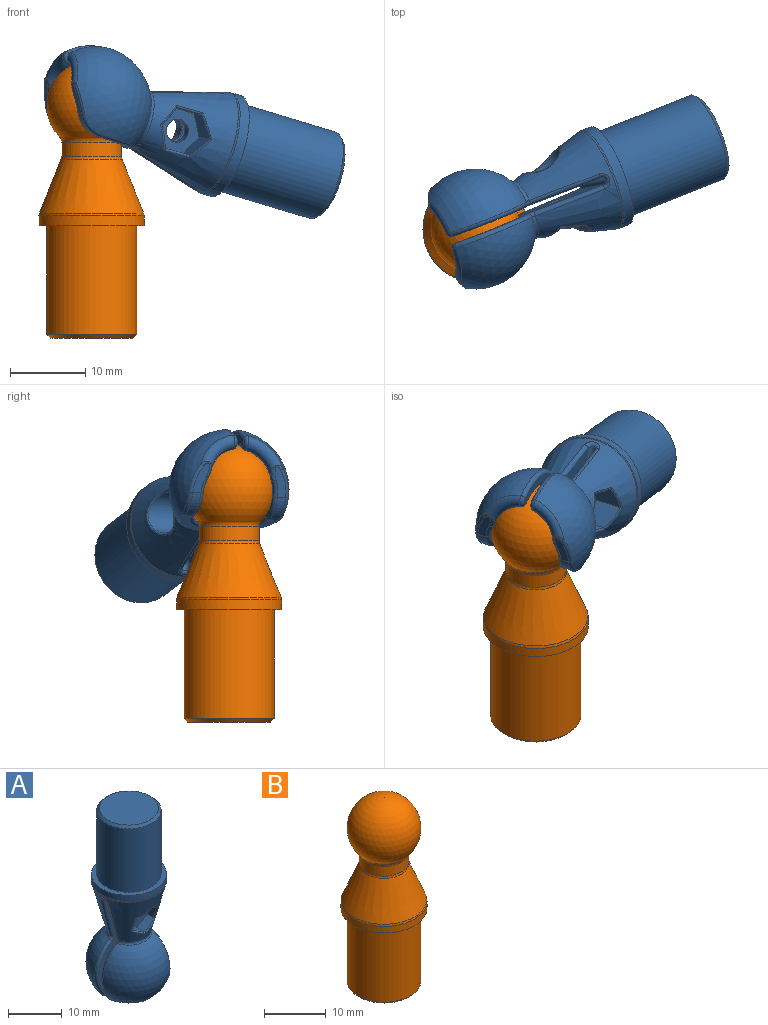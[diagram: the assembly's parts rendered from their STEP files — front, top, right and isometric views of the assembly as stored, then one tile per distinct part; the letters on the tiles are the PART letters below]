
ASSEMBLY  parts=2 mates=1
PART A: 86 faces, bbox 16.3x16.2x40.7 mm
  f0: cone r=7mm half-angle=14.5deg, axis (0,0,1), area 280.4mm2, adj f32,f46,f47,f51,f52,f53,f54,f55
  f1: sphere r=6mm, area 115.3mm2, adj f2,f71,f73,f75,f76
  f2: torus R=5.39mm, axis (0,0,1), area 16.5mm2, adj f1,f3,f68,f70
  f3: sphere r=8mm, area 177.2mm2, adj f2,f58,f59,f62,f63,f64,f65,f67
  f4: plane 6.59x5.73mm, normal (1,0,0), area 9.8mm2, adj f13,f59,f63,f69,f72,f76
  f5: sphere r=6mm, area 115.3mm2, adj f6,f33,f34,f36,f40
  f6: torus R=5.39mm, axis (0,0,1), area 16.5mm2, adj f5,f7,f35,f43
  f7: sphere r=8mm, area 177.2mm2, adj f6,f37,f39,f42,f45,f46,f47,f48
  f8: cylinder r=7mm len=14mm, axis (0,0,1), area 60.4mm2, adj f9,f32
  f9: plane 14x14mm, normal (0,0,1), area 40.8mm2, adj f8,f10
  f10: cylinder r=6mm len=14.5mm, axis (0,0,1), area 546.6mm2, adj f9,f31
  f11: plane 11x11mm, normal (0,0,1), area 95mm2, adj f31
  f12: cylinder r=4mm len=3.58mm, axis (0,-1,0), area 5.1mm2, adj f15,f16,f34,f39
  f13: cylinder r=4mm len=3.58mm, axis (0,-1,0), area 5.1mm2, adj f4,f14,f64,f75
  f14: plane 3.68x1.95mm, normal (0.45,0,-0.89), area 4.5mm2, adj f13,f67,f70,f73
  f15: plane 3.68x1.95mm, normal (0.45,0,-0.89), area 4.5mm2, adj f12,f33,f35,f37
  f16: plane 6.59x5.74mm, normal (1,0,0), area 9.8mm2, adj f12,f36,f41,f42,f44,f45
  f17: plane 22.15x13.62mm, normal (0,1,0), area 103.3mm2, adj f19,f40,f41,f43,f44,f48,f50,f51
  f18: plane 22.15x13.62mm, normal (0,-1,0), area 103.3mm2, adj f19,f56,f57,f60,f61,f65,f68,f69
  f19: cylinder r=0.5mm len=12.02mm, axis (-1,0,0), area 18.9mm2, adj f17,f18,f54,f55
  f20: cylinder r=2.8mm len=5.6mm, axis (0,1,0), area 51.8mm2, adj f21,f83
  f21: plane 5.6x5.6mm, normal (0,1,0), area 17.1mm2, adj f20,f22
  f22: cylinder r=1.55mm len=3.1mm, axis (0,1,0), area 12.7mm2, adj f21,f85
  f23: cylinder r=1.55mm len=3.1mm, axis (0,1,0), area 12.7mm2, adj f24,f84
  f24: plane 6.47x5.6mm, normal (0,-1,0), area 19.6mm2, adj f23,f25,f26,f27,f28,f29,f30
  f25: plane 3.23x2.64mm, normal (1,0,0), area 6.9mm2, adj f24,f26,f30,f82
  f26: plane 2.8x2.26mm, normal (0.5,0,0.87), area 6.8mm2, adj f24,f25,f27,f80,f82
  f27: plane 2.8x2.26mm, normal (-0.5,0,0.87), area 6.8mm2, adj f24,f26,f28,f77,f78
  f28: plane 3.23x2.64mm, normal (-1,0,0), area 6.9mm2, adj f24,f27,f29,f77
  f29: plane 4x2.83mm, normal (-0.5,0,-0.87), area 11.4mm2, adj f24,f28,f30,f77,f79
  f30: plane 4x2.83mm, normal (0.5,0,-0.87), area 11.4mm2, adj f24,f25,f29,f81,f82
  f31: cone r=5.5mm half-angle=45deg, axis (0,0,-1), area 25.5mm2, adj f10,f11
  f32: torus R=6mm, axis (0,0,-1), area 11.1mm2, adj f0,f8
  f33: torus R=5.48mm, axis (0.45,0,-0.89), area 2.4mm2, adj f5,f15,f34,f35
  f34: torus R=3.5mm, axis (0,1,0), area 4.4mm2, adj f5,f12,f33,f36
  f35: bspline ~2.56x2.02mm, area 1.7mm2, adj f6,f15,f33,f37
  f36: torus R=5.48mm, axis (-1,0,0), area 7.6mm2, adj f5,f16,f34,f38
  f37: torus R=6.63mm, axis (0.45,0,-0.89), area 2.2mm2, adj f7,f15,f35,f39
  f38: sphere r=0.5mm, area 0.4mm2, adj f36,f40,f41
  f39: torus R=3.5mm, axis (0,1,0), area 2.3mm2, adj f7,f12,f37,f42
  f40: torus R=6.42mm, axis (0,-1,0), area 12.4mm2, adj f5,f17,f38,f43
  f41: cylinder r=0.5mm len=0.67mm, axis (0,0,1), area 0.5mm2, adj f16,f17,f38,f44
  f42: torus R=6.63mm, axis (-1,0,0), area 4.4mm2, adj f7,f16,f39,f45
  f43: bspline ~1.97x1.8mm, area 1.9mm2, adj f6,f17,f40,f48
  f44: bspline ~0.96x0.87mm, area 0.7mm2, adj f16,f17,f41,f49
  f45: bspline ~1.28x0.59mm, area 0.5mm2, adj f7,f16,f42,f49
  f46: bspline ~0.92x0.62mm, area 0.4mm2, adj f0,f7,f47,f49
  f47: torus R=4.58mm, axis (0,0,-1), area 5.8mm2, adj f0,f7,f46,f50
  f48: torus R=7.43mm, axis (0,-1,0), area 11.4mm2, adj f7,f17,f43,f50
  f49: bspline ~1.65x0.88mm, area 0.8mm2, adj f44,f45,f46,f51
  f50: bspline ~1.33x0.87mm, area 0.7mm2, adj f17,f47,f48,f52
  f51: bspline ~1.11x1.04mm, area 0.9mm2, adj f0,f17,f49,f53
  f52: bspline ~18.22x5.33mm, area 8.8mm2, adj f0,f17,f50,f54
  f53: bspline ~11.75x3.63mm, area 8.2mm2, adj f0,f17,f51,f55
  f54: bspline ~2.16x1.22mm, area 1.7mm2, adj f0,f19,f52,f56
  f55: bspline ~2.16x1.22mm, area 1.7mm2, adj f0,f19,f53,f57
  f56: bspline ~13.51x4.11mm, area 8.8mm2, adj f0,f18,f54,f60
  f57: bspline ~11.75x3.63mm, area 8.2mm2, adj f0,f18,f55,f61
  f58: torus R=4.58mm, axis (0,0,-1), area 5.8mm2, adj f0,f3,f60,f62
  f59: torus R=6.63mm, axis (-1,0,0), area 4.4mm2, adj f3,f4,f63,f64
  f60: bspline ~1.35x0.82mm, area 0.7mm2, adj f18,f56,f58,f65
  f61: bspline ~1.11x1.04mm, area 0.9mm2, adj f0,f18,f57,f66
  f62: bspline ~0.92x0.62mm, area 0.4mm2, adj f0,f3,f58,f66
  f63: bspline ~1.28x0.59mm, area 0.5mm2, adj f3,f4,f59,f66
  f64: torus R=3.5mm, axis (0,-1,0), area 2.3mm2, adj f3,f13,f59,f67
  f65: torus R=7.43mm, axis (0,-1,0), area 11.4mm2, adj f3,f18,f60,f68
  f66: bspline ~1.65x0.88mm, area 0.8mm2, adj f61,f62,f63,f69
  f67: torus R=6.63mm, axis (0.45,0,-0.89), area 2.2mm2, adj f3,f14,f64,f70
  f68: bspline ~1.87x1.8mm, area 1.9mm2, adj f2,f18,f65,f71
  f69: bspline ~0.96x0.87mm, area 0.7mm2, adj f4,f18,f66,f72
  f70: bspline ~2.56x2.02mm, area 1.7mm2, adj f2,f14,f67,f73
  f71: torus R=6.42mm, axis (0,-1,0), area 12.4mm2, adj f1,f18,f68,f74
  f72: cylinder r=0.5mm len=0.67mm, axis (0,0,-1), area 0.5mm2, adj f4,f18,f69,f74
  f73: torus R=5.48mm, axis (0.45,0,-0.89), area 2.4mm2, adj f1,f14,f70,f75
  f74: sphere r=0.5mm, area 0.5mm2, adj f71,f72,f76
  f75: torus R=3.5mm, axis (0,-1,0), area 4.4mm2, adj f1,f13,f73,f76
  f76: torus R=5.48mm, axis (-1,0,0), area 7.6mm2, adj f1,f4,f74,f75
  f77: bspline ~5.04x1.9mm, area 1.5mm2, adj f0,f27,f28,f29,f78,f79
  f78: bspline ~4.36x2.68mm, area 1.4mm2, adj f0,f27,f77,f80
  f79: bspline ~4.23x2.51mm, area 1.1mm2, adj f0,f29,f77,f81
  f80: bspline ~4.36x2.68mm, area 1.4mm2, adj f0,f26,f78,f82
  f81: bspline ~4.23x2.51mm, area 1.1mm2, adj f0,f30,f79,f82
  f82: bspline ~5.04x1.9mm, area 1.5mm2, adj f0,f25,f26,f30,f80,f81
  f83: bspline ~6.23x6.01mm, area 7.1mm2, adj f0,f20
  f84: torus R=1.75mm, axis (0,-1,0), area 3.2mm2, adj f17,f23
  f85: torus R=1.75mm, axis (0,-1,0), area 3.2mm2, adj f18,f22
PART B: 11 faces, bbox 15.2x15.2x37 mm
  f0: cylinder r=6mm len=14.5mm, axis (0,0,1), area 546.6mm2, adj f1,f7
  f1: plane 14x14mm, normal (0,0,-1), area 40.8mm2, adj f0,f2
  f2: cylinder r=7mm len=14mm, axis (0,0,1), area 57.5mm2, adj f1,f8
  f3: cone r=4mm half-angle=21.8deg, axis (0,0,-1), area 265.8mm2, adj f8,f9
  f4: cylinder r=4mm len=8mm, axis (0,0,1), area 48mm2, adj f9,f10
  f5: sphere r=6mm, area 384.5mm2, adj f10
  f6: plane 11x11mm, normal (0,0,-1), area 95mm2, adj f7
  f7: cone r=6mm half-angle=45deg, axis (0,0,1), area 25.5mm2, adj f0,f6
  f8: torus R=6mm, axis (0,0,-1), area 16.7mm2, adj f2,f3
  f9: torus R=5mm, axis (0,0,1), area 9.6mm2, adj f3,f4
  f10: torus R=5mm, axis (0,0,1), area 20mm2, adj f4,f5
PLACE A rot(axis=(-0.16,0.97,0.16),107.7deg) t=(-14.32,-5.69,20.32)mm
PLACE B at identity fixed
MATE ball B.f9 <-> A.f47  axis (0,0,1) through (0,0,16)mm
